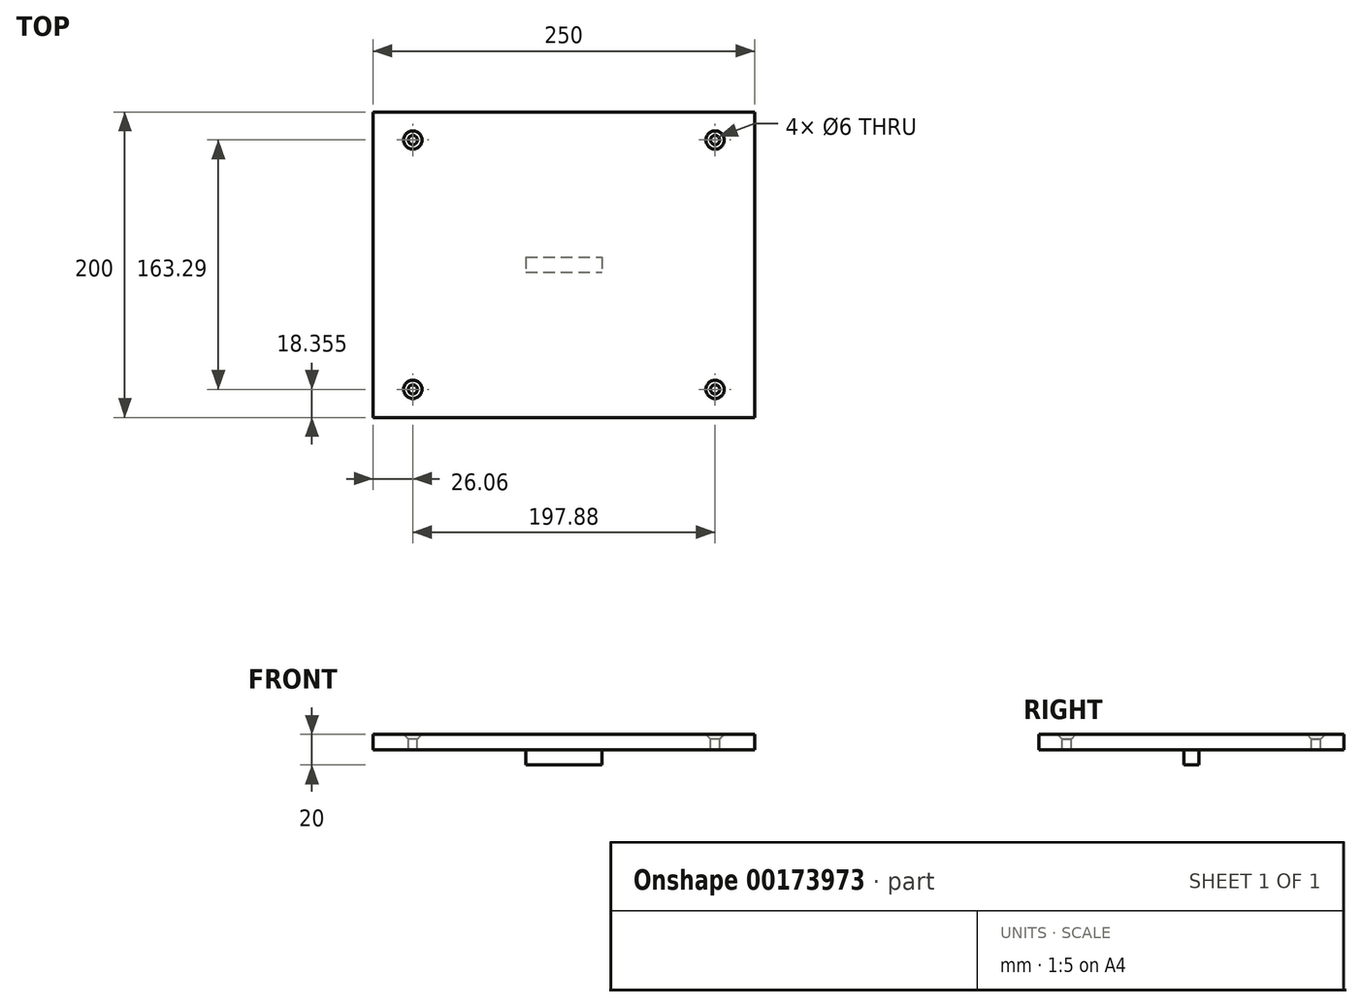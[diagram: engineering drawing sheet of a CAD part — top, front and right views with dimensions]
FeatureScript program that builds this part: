
annotation { "Feature Type Name" : "Feature", "Feature Type Description" : "" }
export const myFeature = defineFeature(function(context is Context, id is Id, definition is map)
    precondition{}
    {
        {
            var Q0;
            Q0=qCreatedBy(makeId("Top.planeOp"),FACE);
            var sketch = newSketch(context, id + "F0", { "sketchPlane" : qUnion([Q0])});
            skLineSegment(sketch, "E0.bottom", {"start": v(125, -100) * mm, "end": v(-125, -100) * mm});
            skLineSegment(sketch, "E0.top", {"start": v(125, 100) * mm, "end": v(-125, 100) * mm});
            skLineSegment(sketch, "E0.left", {"start": v(125, -100) * mm, "end": v(125, 100) * mm});
            skLineSegment(sketch, "E0.right", {"start": v(-125, -100) * mm, "end": v(-125, 100) * mm});
            skPoint(sketch, "E0.middle", {"position": v(0, 0) * mm});
            skLineSegment(sketch, "E1", {"start": v(0, 0) * mm, "end": v(11.67, -100) * mm, "construction": true});
            skLineSegment(sketch, "E2", {"start": v(0, 0) * mm, "end": v(-11.67, 100) * mm, "construction": true});
            skLineSegment(sketch, "E3", {"start": v(0, 0) * mm, "end": v(125, 0) * mm, "construction": true});
            skLineSegment(sketch, "E4", {"start": v(0, 0) * mm, "end": v(-125, 0) * mm, "construction": true});
            skSolve(sketch);
        }
        {
            var Q0;
            Q0=makeQuery(id+"F0.imprint","IMPRINT",FACE,{"disambiguationData":[TD([[makeQuery(id+"F0.imprint","IMPRINT",EDGE,{"derivedFrom":sQuery(id+"F0.wireOp",EDGE,"E0.bottom")}),-1.0]])]});
            extrude(context, id + "F1", {"entities" : qUnion([Q0]), "depth" : 10 * mm});
        }
        {
            var Q0;
            Q0=makeQuery(id+"F1.opExtrude","CAP_FACE",FACE,{"disambiguationData":[OSD([sQuery(id+"F0.wireOp",EDGE,"E0.bottom"),sQuery(id+"F0.wireOp",EDGE,"E0.top"),sQuery(id+"F0.wireOp",EDGE,"E0.left"),sQuery(id+"F0.wireOp",EDGE,"E0.right")])],"isStart":false});
            var sketch = newSketch(context, id + "F2", { "sketchPlane" : qUnion([Q0])});
            skLineSegment(sketch, "E5.bottom", {"start": v(-98.94, 81.64) * mm, "end": v(98.94, 81.64) * mm, "construction": true});
            skLineSegment(sketch, "E5.top", {"start": v(-98.94, -81.64) * mm, "end": v(98.94, -81.64) * mm, "construction": true});
            skLineSegment(sketch, "E5.left", {"start": v(-98.94, 81.64) * mm, "end": v(-98.94, -81.64) * mm, "construction": true});
            skLineSegment(sketch, "E5.right", {"start": v(98.94, 81.64) * mm, "end": v(98.94, -81.64) * mm, "construction": true});
            skPoint(sketch, "E5.middle", {"position": v(0, 0) * mm});
            skLineSegment(sketch, "E6", {"start": v(0, 81.64) * mm, "end": v(0, -81.64) * mm, "construction": true});
            skSolve(sketch);
        }
        {
            var Q0;
            Q0=sQuery(id+"F2.wireOp",VERTEX,"E5.left.start");
            var Q1;
            Q1=sQuery(id+"F2.wireOp",VERTEX,"E5.right.start");
            var Q2;
            Q2=sQuery(id+"F2.wireOp",VERTEX,"E5.top.end");
            var Q3;
            Q3=sQuery(id+"F2.wireOp",VERTEX,"E5.left.end");
            var Q4;
            Q4=makeQuery(id+"F1.opExtrude","SWEPT_BODY",BODY,{"disambiguationData":[OSD([sQuery(id+"F0.wireOp",EDGE,"E0.bottom"),sQuery(id+"F0.wireOp",EDGE,"E0.top"),sQuery(id+"F0.wireOp",EDGE,"E0.left"),sQuery(id+"F0.wireOp",EDGE,"E0.right")])]});
            hole(context, id + "F3", {"style" : HoleStyle.C_SINK, "endStyle" : HoleEndStyle.THROUGH, "standardTappedOrClearance" : lookupTablePath({ "standard" : "ISO", "size" : "6", "type" : "Drilled" }), "standardBlindInLast" : lookupTablePath({ "standard" : "ISO", "size" : "6", "type" : "Drilled" }), "holeDiameter" : 6 * mm, "cSinkDiameter" : 12 * mm, "cSinkAngle" : 90 * degree, "startFromSketch" : true, "locations" : qUnion([Q0, Q1, Q2, Q3]), "scope" : qUnion([Q4]), "isTappedThrough" : true});
        }
        {
            var Q0;
            Q0=qCreatedBy(makeId("Top.planeOp"),FACE);
            var sketch = newSketch(context, id + "F4", { "sketchPlane" : qUnion([Q0])});
            skLineSegment(sketch, "E7.bottom", {"start": v(-25, 5) * mm, "end": v(25, 5) * mm});
            skLineSegment(sketch, "E7.top", {"start": v(-25, -5) * mm, "end": v(25, -5) * mm});
            skLineSegment(sketch, "E7.left", {"start": v(-25, 5) * mm, "end": v(-25, -5) * mm});
            skLineSegment(sketch, "E7.right", {"start": v(25, 5) * mm, "end": v(25, -5) * mm});
            skPoint(sketch, "E7.middle", {"position": v(0, 0) * mm});
            skSolve(sketch);
        }
        {
            var Q0;
            Q0 = qSketchRegion(id + "F4", true);
            extrude(context, id + "F5", {"entities" : qUnion([Q0]), "operationType" : NewBodyOperationType.ADD, "oppositeDirection" : true, "depth" : 10 * mm});
        }
    });
